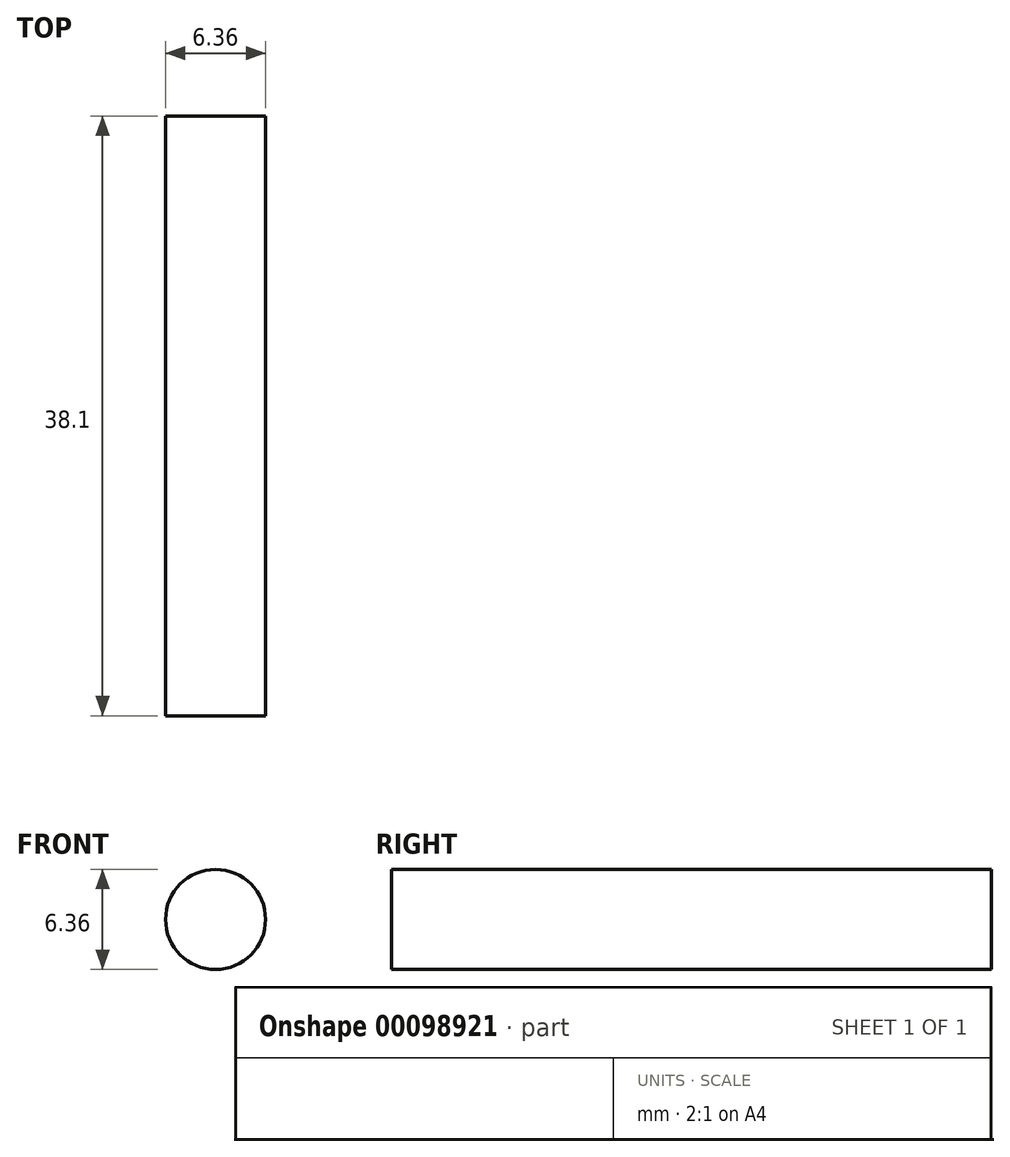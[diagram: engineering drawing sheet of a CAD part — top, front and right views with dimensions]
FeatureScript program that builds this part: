
annotation { "Feature Type Name" : "Feature", "Feature Type Description" : "" }
export const myFeature = defineFeature(function(context is Context, id is Id, definition is map)
    precondition{}
    {
        {
            var Q0;
            Q0=qCreatedBy(makeId("Front.planeOp"),FACE);
            var sketch = newSketch(context, id + "F0", { "sketchPlane" : qUnion([Q0])});
            skCircle(sketch, "E0", {"center": v(0, 0) * mm, "radius": 3.18 * mm});
            skSolve(sketch);
        }
        {
            var Q0;
            Q0=makeQuery(id+"F0.imprint","IMPRINT",FACE,{"disambiguationData":[TD([[makeQuery(id+"F0.imprint","IMPRINT",EDGE,{"derivedFrom":sQuery(id+"F0.wireOp",EDGE,"E0")}),1.0]])]});
            extrude(context, id + "F1", {"entities" : qUnion([Q0]), "depth" : 38.1 * mm});
        }
    });
